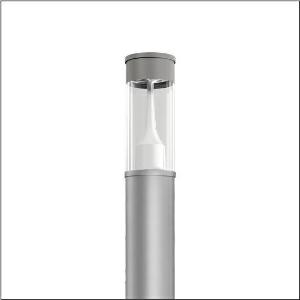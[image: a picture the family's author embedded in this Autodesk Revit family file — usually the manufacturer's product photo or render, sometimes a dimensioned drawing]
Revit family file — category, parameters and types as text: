
# Revit family: city-light_260_iq___pl1_2s_5xa5295jf14h_6623
name_source: partatom
category: Lighting Fixtures
units: mm (PartAtom-declared; Revit-internal decimal feet)

## family parameters
Cut with Voids When Loaded = No
Host = Face
Light Source = No
Part Type = Normal
Room Calculation Point = No
Round Connector Dimension = Use Diameter
Shared = No

## types (1)
- --- (1 x LED, 4740 lm, 19.3 W, 3000K)
    Apparent Load = 19 VA
    CIE Flux Codes = 23 62 94 96 100
    Color Rendering = 70
    Color Temperature = 3000K
    Default Elevation = 1800 mm
    Description = City-Light 260 iQ, light pillar, Module 540 iQ-SR, primary light control with 3 zone facetted reflector, of plastic, silver coated, highly specular, structured, primary optical cover: cover, of PMMA, transparent, light distribution: PL1.2s, primary light characteristic: symmetric, LED, High Power LED, rated luminous flux: 2.970lm, luminous efficacy: 154lm/W, light colour: 730, colour temperature: 3000K, control gear: ECG iQ, control: Auto-Match, Temp-Guard, Lumen-Switch, Night-Set, Smart-Wire, Light-Fading, Desk-Remote (wireless, voltage-free reading and setting of iQ features in the workshop via application-optimized NFC function/RFID function), optimised constant luminous flux control (CLO 2.0), Street-Remote, presetting dimming logarithmic, with terminal, 6-pole, max. 2.5mm², mains connection: 230..240V, AC, 50/60Hz, start of lifetime: 19W, end of service life: 21W, reduction: 10W, luminaire housing, cylindrical, of extruded aluminium section, coated, Siteco® metallic grey (DB 702S), length: 2.600mm, diameter: 200mm, Module 540 iQ-SR, traffic white (RAL 9016), equipment: standard, protection rating (complete): IP65, insulation class (complete): insulation class II (safety insulation), certification: CE, ENEC, VDE, packaging unit: 1 piece

Light Distribution: PL1.2s
    Height = 500 mm
    Lamp = 1 x LED
    Lamp Light Flux = 4740 lm
    Lamp Power = 19.3 W
    Lamp count = 1
    Length = 200 mm  [stored 0.656168 ft]
    Luminous efficacy = 246 lm/W
    Manufacturer = Siteco
    ModVariant = No
    Model = 5XA5295JF14H
    Mounting Place = Floor
    Mounting Type = Freestanding
    Number of Poles = 1
    OnlyDefault = Yes
    Power Factor = 1
    Product Name = City-Light 260 iQ | PL1.2s
    Product group = light pillar
    ProductGroupID = 1303
    Protection Class = Protection class II
    Protection Degree = IP 65
    RLX_Detail_Level = 1
    RLX_Emergency_Light_Flux = 0 lm
    RLX_Emergency_Type = 0
    RLX_Emergency_Type_DB = No
    RlxData = <blob elided: 28865 chars, md5=8c2f4605>
    Socket = socket
    Standby Power = 0 W
    System Light Flux = 4740 lm
    System Power = 19 W
    Type Comments = factory setting: luminous flux: 100 % | dim-lin: 254 | 403 mA
    Type Image = l_1006920.jpg
    URL = http://relux.com
    VarID = @adj_094615
    Voltage = 0 V
    Weight = 0.00 kg
    Width = 0 mm  [stored 0 ft]

note: [stored X ft] marks values corroborated as IEEE doubles in the binary element streams (Revit-internal decimal feet)

## geometry (parser evidence)
native form markers: Blend x4, Sweep x8
no freeform markers — native parametric forms only
